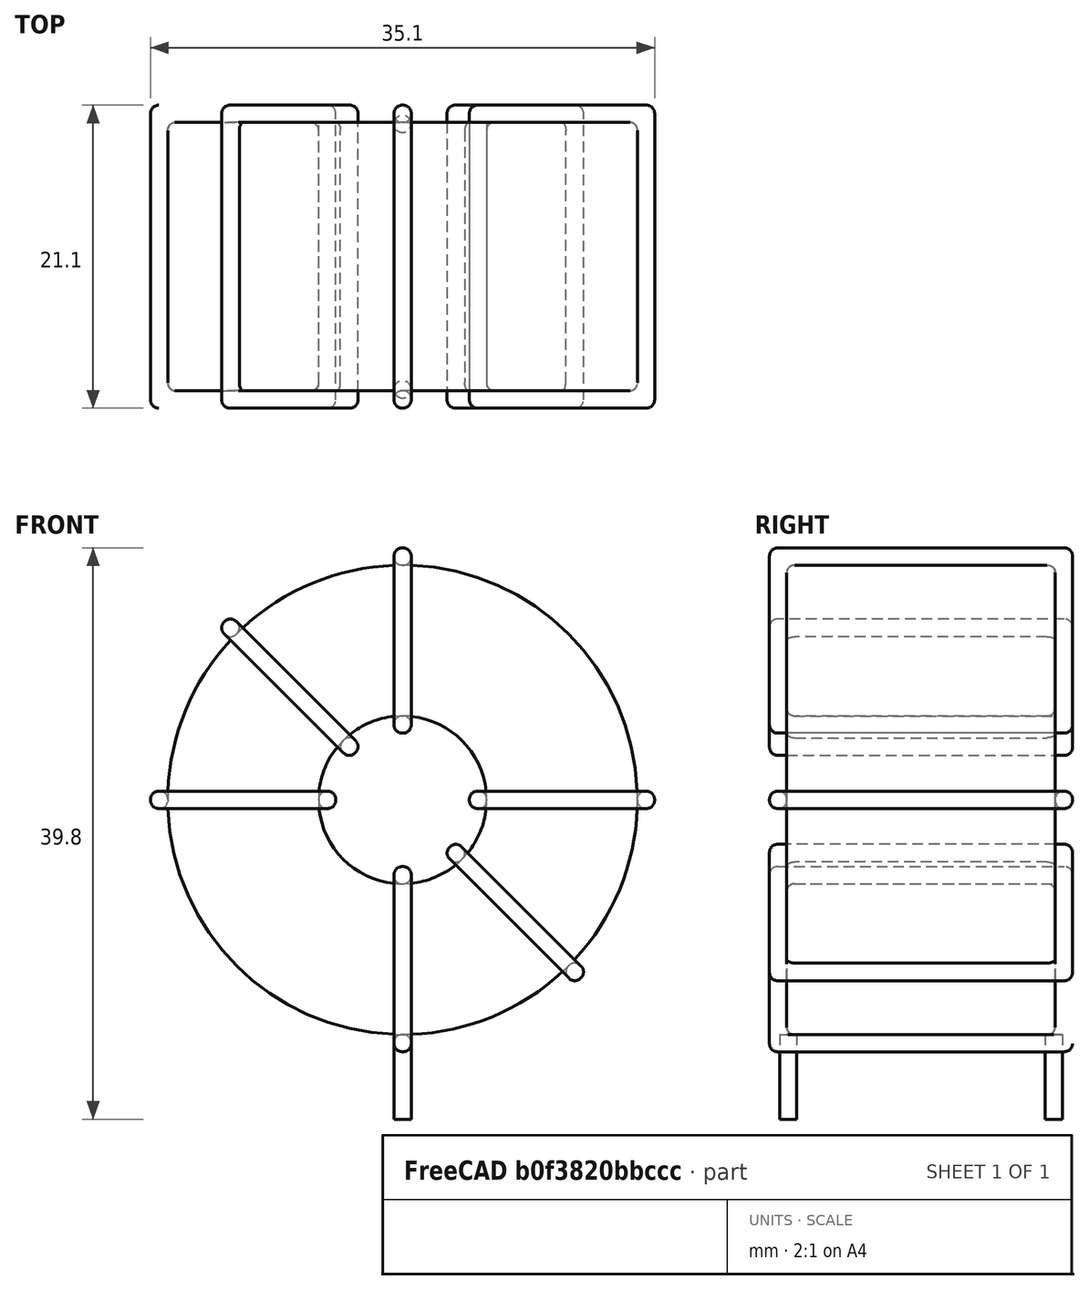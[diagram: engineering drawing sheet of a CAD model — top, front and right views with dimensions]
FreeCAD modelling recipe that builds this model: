
FCSTD DOCUMENT  (FreeCAD 0.16R6703 (Git))
Label: L_Toroid_Vertical_L35.1mm_W21.1mm_P18.50mm_Vishay_TJ6
License: All rights reserved
LicenseURL: http://en.wikipedia.org/wiki/All_rights_reserved
objects: Sketcher::SketchObject×6, PartDesign::Pad×6, PartDesign::Fillet×5, Spreadsheet::Sheet×1
note: 23 computed .brp shape members not serialized (recipe doc carries the construction recipe); baked Part::Feature solids carry a one-line shape summary decoded from their .brp

FEATURE [Spreadsheet::Sheet] Spreadsheet  label="dimensions"
  cells = A1=Wx; B1(Wx)=35.1; C1(WW)=11.7; D1=35.1; A2=Wy; B2(Wy)=21.1; D2=21.1; A3=RM; B3(RMx)=18.5; C3(RMy)=0; A4=d_wire; B4(d_wire)=1.2; A5=H; B5(H)=35.1; A6=offsetx; B6(offsetx)=17.55
FEATURE [Sketcher::SketchObject] Sketch
  Placement = pos=(0,-9.25,0) rot=(1,0,0;1.5708rad)
  expr: Placement.Base.y = -Spreadsheet.RMx / 2
  expr: Constraints[0] = Spreadsheet.Wx / 2 - Spreadsheet.d_wire
  expr: Constraints[4] = Spreadsheet.WW / 2
  expr: Constraints[2] = Spreadsheet.Wx / 2 + Spreadsheet.d_wire + 0.5
  sketch-geometry (2):
    g0: Circle CenterX=0 CenterY=19.25 CenterZ=0 NormalX=0 NormalY=0 NormalZ=1 Radius=16.35
    g1: Circle CenterX=0 CenterY=19.25 CenterZ=0 NormalX=0 NormalY=0 NormalZ=1 Radius=5.85
  constraints (5):
    c: Radius(g0) = 16.35
    c: DistanceX(g-1,g0) = 0
    c: DistanceY(g-1,g0) = 19.25
    c: Coincident(g1,g0)
    c: Radius(g1) = 5.85
FEATURE [PartDesign::Pad] Pad
  Length = 18.7
  Length2 = 100
  Midplane = true
  Placement = pos=(0,-9.25,0) rot=(1,0,0;1.5708rad)
  Sketch = -> Sketch
  Type = 0
  expr: Length = Spreadsheet.Wy - 2 * Spreadsheet.d_wire
FEATURE [Sketcher::SketchObject] Sketch001
  Placement = pos=(0,0,1.7) rot=(0,0,1;0rad)
  expr: Placement.Base.z = 0.5 + Spreadsheet.d_wire
  expr: Constraints[4] = Spreadsheet.RMy
  expr: Constraints[2] = -Spreadsheet.RMx
  expr: Constraints[1] = Spreadsheet.d_wire / 2
  sketch-geometry (2):
    g0: Circle CenterX=0 CenterY=0 CenterZ=0 NormalX=0 NormalY=0 NormalZ=1 Radius=0.6
    g1: Circle CenterX=0 CenterY=-18.5 CenterZ=0 NormalX=0 NormalY=0 NormalZ=1 Radius=0.6
  constraints (5):
    c: Equal(g0,g1)
    c: Radius(g0) = 0.6
    c: DistanceY(g-1,g1) = -18.5
    c: Coincident(g0,g-1)
    c: DistanceX(g-1,g1) = 0
FEATURE [PartDesign::Pad] Pad001
  Length = 1.2
  Length2 = 4.7
  Placement = pos=(0,0,1.7) rot=(0,0,1;0rad)
  Reversed = true
  Sketch = -> Sketch001
  Type = 4
  expr: Length2 = 3.5 + Spreadsheet.d_wire
  expr: Length = Spreadsheet.d_wire
FEATURE [PartDesign::Fillet] Fillet
  Base = -> Pad [Edge6,Edge3,Edge2]
  Placement = pos=(0,-9.25,0) rot=(1,0,0;1.5708rad)
  Radius = 0.5
FEATURE [Sketcher::SketchObject] Sketch003
  Placement = pos=(0,1.3,19.25) rot=(1,0,0;3.14159rad)
  expr: Constraints[18] = Spreadsheet.d_wire
  expr: Constraints[16] = Spreadsheet.d_wire
  expr: Constraints[19] = Spreadsheet.d_wire
  expr: Constraints[17] = Spreadsheet.d_wire
  expr: Placement.Base.y = -1 * (Spreadsheet.RMx - Spreadsheet.Wy) / 2
  expr: Constraints[21] = (Spreadsheet.Wx - Spreadsheet.WW) / 2 - Spreadsheet.d_wire
  expr: Constraints[22] = Spreadsheet.Wx / 2 - Spreadsheet.d_wire
  expr: Constraints[43] = Spreadsheet.d_wire
  expr: Constraints[48] = Spreadsheet.Wx - Spreadsheet.d_wire * 2
  expr: Constraints[49] = Spreadsheet.Wy
  expr: Placement.Base.z = Spreadsheet.Wx / 2 + Spreadsheet.d_wire + 0.5
  sketch-geometry (16):
    g0: LineSegment StartX=-4.65 StartY=0 StartZ=0 EndX=-17.55 EndY=0 EndZ=0
    g1: LineSegment StartX=-17.55 StartY=0 StartZ=0 EndX=-17.55 EndY=21.1 EndZ=0
    g2: LineSegment StartX=-17.55 StartY=21.1 StartZ=0 EndX=-4.65 EndY=21.1 EndZ=0
    g3: LineSegment StartX=-4.65 StartY=21.1 StartZ=0 EndX=-4.65 EndY=0 EndZ=0
    g4: LineSegment StartX=-16.35 StartY=19.9 StartZ=0 EndX=-5.85 EndY=19.9 EndZ=0
    g5: LineSegment StartX=-5.85 StartY=19.9 StartZ=0 EndX=-5.85 EndY=1.2 EndZ=0
    g6: LineSegment StartX=-5.85 StartY=1.2 StartZ=0 EndX=-16.35 EndY=1.2 EndZ=0
    g7: LineSegment StartX=-16.35 StartY=1.2 StartZ=0 EndX=-16.35 EndY=19.9 EndZ=0
    g8: LineSegment StartX=4.65 StartY=21.1 StartZ=0 EndX=17.55 EndY=21.1 EndZ=0
    g9: LineSegment StartX=17.55 StartY=21.1 StartZ=0 EndX=17.55 EndY=0 EndZ=0
    g10: LineSegment StartX=17.55 StartY=0 StartZ=0 EndX=4.65 EndY=0 EndZ=0
    g11: LineSegment StartX=4.65 StartY=0 StartZ=0 EndX=4.65 EndY=21.1 EndZ=0
    g12: LineSegment StartX=5.85 StartY=19.9 StartZ=0 EndX=16.35 EndY=19.9 EndZ=0
    g13: LineSegment StartX=16.35 StartY=19.9 StartZ=0 EndX=16.35 EndY=1.2 EndZ=0
    g14: LineSegment StartX=16.35 StartY=1.2 StartZ=0 EndX=5.85 EndY=1.2 EndZ=0
    g15: LineSegment StartX=5.85 StartY=1.2 StartZ=0 EndX=5.85 EndY=19.9 EndZ=0
  constraints (50):
    c: Horizontal(g0)
    c: Coincident(g1,g0)
    c: Vertical(g1)
    c: Coincident(g2,g1)
    c: Horizontal(g2)
    c: Coincident(g3,g2)
    c: Coincident(g3,g0)
    c: Vertical(g3)
    c: Coincident(g4,g5)
    c: Coincident(g5,g6)
    c: Coincident(g6,g7)
    c: Coincident(g7,g4)
    c: Horizontal(g4)
    c: Horizontal(g6)
    c: Vertical(g5)
    c: Vertical(g7)
    c: DistanceX(g1,g4) = 1.2
    c: DistanceY(g4,g1) = 1.2
    c: DistanceX(g5,g0) = 1.2
    c: DistanceY(g0,g5) = 1.2
    c: DistanceY(g-1,g0) = 0
    c: DistanceX(g6,g6) = 10.5
    c: DistanceX(g6,g-1) = 16.35
    c: Coincident(g8,g9)
    c: Coincident(g9,g10)
    c: Coincident(g10,g11)
    c: Coincident(g11,g8)
    c: Horizontal(g8)
    c: Horizontal(g10)
    c: Vertical(g9)
    c: Vertical(g11)
    c: Coincident(g12,g13)
    c: Coincident(g13,g14)
    c: Coincident(g14,g15)
    c: Coincident(g15,g12)
    c: Horizontal(g12)
    c: Horizontal(g14)
    c: Vertical(g13)
    c: Vertical(g15)
    c: DistanceY(g8,g2) = 0
    c: DistanceY(g10,g0) = 0
    c: DistanceY(g14,g5) = 0
    c: DistanceY(g12,g4) = 0
    c: DistanceX(g8,g12) = 1.2
    c: Equal(g8,g2)
    c: Equal(g12,g4)
    c: Equal(g9,g1)
    c: Equal(g13,g7)
    c: DistanceX(g4,g12) = 32.7
    c: DistanceY(g0,g1) = 21.1
FEATURE [PartDesign::Pad] Pad002
  Length = 1.2
  Length2 = 100
  Midplane = true
  Placement = pos=(0,1.3,19.25) rot=(1,0,0;3.14159rad)
  Sketch = -> Sketch003
  Type = 0
  expr: Length = Spreadsheet.d_wire
FEATURE [PartDesign::Fillet] Fillet001
  Base = -> Pad002 [Edge38,Edge41,Edge42,Edge43,Edge29,Edge32,Edge33,Edge34,Edge25,Edge35,Edge36,Edge13,Edge14,Edge15,Edge16,Edge17,Edge18,Edge19,Edge1,Edge2,Edge3,Edge4,Edge5,Edge6,Edge7,Edge37,Edge39,Edge40,Edge20,Edge23,Edge24,Edge21,Edge22,Edge8,Edge9,Edge10,Edge11,Edge12,Edge26,Edge27,+8 more]
  Placement = pos=(0,1.3,19.25) rot=(1,0,0;3.14159rad)
  Radius = 0.564
  expr: Radius = Spreadsheet.d_wire * 0.47
FEATURE [Sketcher::SketchObject] Sketch004
  Placement = pos=(0,1.3,19.25) rot=(0.92388,0,0.382683;3.14159rad)
  expr: Constraints[18] = Spreadsheet.d_wire
  expr: Constraints[16] = Spreadsheet.d_wire
  expr: Constraints[19] = Spreadsheet.d_wire
  expr: Constraints[17] = Spreadsheet.d_wire
  expr: Placement.Base.y = -1 * (Spreadsheet.RMx - Spreadsheet.Wy) / 2
  expr: Constraints[21] = (Spreadsheet.Wx - Spreadsheet.WW) / 2 - Spreadsheet.d_wire
  expr: Constraints[22] = Spreadsheet.Wx / 2 - Spreadsheet.d_wire
  expr: Constraints[43] = Spreadsheet.d_wire
  expr: Constraints[48] = Spreadsheet.Wx - 2 * Spreadsheet.d_wire
  expr: Constraints[49] = Spreadsheet.Wy
  expr: Placement.Base.z = Spreadsheet.Wx / 2 + Spreadsheet.d_wire + 0.5
  sketch-geometry (16):
    g0: LineSegment StartX=-4.65 StartY=0 StartZ=0 EndX=-17.55 EndY=0 EndZ=0
    g1: LineSegment StartX=-17.55 StartY=0 StartZ=0 EndX=-17.55 EndY=21.1 EndZ=0
    g2: LineSegment StartX=-17.55 StartY=21.1 StartZ=0 EndX=-4.65 EndY=21.1 EndZ=0
    g3: LineSegment StartX=-4.65 StartY=21.1 StartZ=0 EndX=-4.65 EndY=0 EndZ=0
    g4: LineSegment StartX=-16.35 StartY=19.9 StartZ=0 EndX=-5.85 EndY=19.9 EndZ=0
    g5: LineSegment StartX=-5.85 StartY=19.9 StartZ=0 EndX=-5.85 EndY=1.2 EndZ=0
    g6: LineSegment StartX=-5.85 StartY=1.2 StartZ=0 EndX=-16.35 EndY=1.2 EndZ=0
    g7: LineSegment StartX=-16.35 StartY=1.2 StartZ=0 EndX=-16.35 EndY=19.9 EndZ=0
    g8: LineSegment StartX=4.65 StartY=21.1 StartZ=0 EndX=17.55 EndY=21.1 EndZ=0
    g9: LineSegment StartX=17.55 StartY=21.1 StartZ=0 EndX=17.55 EndY=0 EndZ=0
    g10: LineSegment StartX=17.55 StartY=0 StartZ=0 EndX=4.65 EndY=0 EndZ=0
    g11: LineSegment StartX=4.65 StartY=0 StartZ=0 EndX=4.65 EndY=21.1 EndZ=0
    g12: LineSegment StartX=5.85 StartY=19.9 StartZ=0 EndX=16.35 EndY=19.9 EndZ=0
    g13: LineSegment StartX=16.35 StartY=19.9 StartZ=0 EndX=16.35 EndY=1.2 EndZ=0
    g14: LineSegment StartX=16.35 StartY=1.2 StartZ=0 EndX=5.85 EndY=1.2 EndZ=0
    g15: LineSegment StartX=5.85 StartY=1.2 StartZ=0 EndX=5.85 EndY=19.9 EndZ=0
  constraints (50):
    c: Horizontal(g0)
    c: Coincident(g1,g0)
    c: Vertical(g1)
    c: Coincident(g2,g1)
    c: Horizontal(g2)
    c: Coincident(g3,g2)
    c: Coincident(g3,g0)
    c: Vertical(g3)
    c: Coincident(g4,g5)
    c: Coincident(g5,g6)
    c: Coincident(g6,g7)
    c: Coincident(g7,g4)
    c: Horizontal(g4)
    c: Horizontal(g6)
    c: Vertical(g5)
    c: Vertical(g7)
    c: DistanceX(g1,g4) = 1.2
    c: DistanceY(g4,g1) = 1.2
    c: DistanceX(g5,g0) = 1.2
    c: DistanceY(g0,g5) = 1.2
    c: DistanceY(g-1,g0) = 0
    c: DistanceX(g6,g6) = 10.5
    c: DistanceX(g6,g-1) = 16.35
    c: Coincident(g8,g9)
    c: Coincident(g9,g10)
    c: Coincident(g10,g11)
    c: Coincident(g11,g8)
    c: Horizontal(g8)
    c: Horizontal(g10)
    c: Vertical(g9)
    c: Vertical(g11)
    c: Coincident(g12,g13)
    c: Coincident(g13,g14)
    c: Coincident(g14,g15)
    c: Coincident(g15,g12)
    c: Horizontal(g12)
    c: Horizontal(g14)
    c: Vertical(g13)
    c: Vertical(g15)
    c: DistanceY(g8,g2) = 0
    c: DistanceY(g10,g0) = 0
    c: DistanceY(g14,g5) = 0
    c: DistanceY(g12,g4) = 0
    c: DistanceX(g8,g12) = 1.2
    c: Equal(g8,g2)
    c: Equal(g12,g4)
    c: Equal(g9,g1)
    c: Equal(g13,g7)
    c: DistanceX(g4,g12) = 32.7
    c: DistanceY(g0,g1) = 21.1
FEATURE [PartDesign::Pad] Pad003
  Length = 1.2
  Length2 = 100
  Midplane = true
  Placement = pos=(0,1.3,19.25) rot=(0.92388,0,0.382683;3.14159rad)
  Sketch = -> Sketch004
  Type = 0
  expr: Length = Spreadsheet.d_wire
FEATURE [PartDesign::Fillet] Fillet002
  Base = -> Pad003 [Edge38,Edge41,Edge42,Edge43,Edge29,Edge32,Edge33,Edge34,Edge25,Edge35,Edge36,Edge13,Edge14,Edge15,Edge16,Edge17,Edge18,Edge19,Edge1,Edge2,Edge3,Edge4,Edge5,Edge6,Edge7,Edge37,Edge39,Edge40,Edge20,Edge23,Edge24,Edge21,Edge22,Edge8,Edge9,Edge10,Edge11,Edge12,Edge26,Edge27,+8 more]
  Placement = pos=(0,1.3,19.25) rot=(0.92388,0,0.382683;3.14159rad)
  Radius = 0.564
  expr: Radius = Spreadsheet.d_wire * 0.47
FEATURE [Sketcher::SketchObject] Sketch005
  Placement = pos=(0,1.3,19.25) rot=(0.92388,0,-0.382683;3.14159rad)
  expr: Constraints[18] = Spreadsheet.d_wire
  expr: Constraints[16] = Spreadsheet.d_wire
  expr: Constraints[19] = Spreadsheet.d_wire
  expr: Constraints[17] = Spreadsheet.d_wire
  expr: Placement.Base.y = -1 * (Spreadsheet.RMx - Spreadsheet.Wy) / 2
  expr: Constraints[21] = (Spreadsheet.Wx - Spreadsheet.WW) / 2 - Spreadsheet.d_wire
  expr: Constraints[22] = Spreadsheet.Wx / 2 - Spreadsheet.d_wire
  expr: Constraints[43] = Spreadsheet.d_wire
  expr: Constraints[48] = Spreadsheet.Wx - 2 * Spreadsheet.d_wire
  expr: Constraints[49] = Spreadsheet.Wy
  expr: Placement.Base.z = Spreadsheet.Wx / 2 + Spreadsheet.d_wire + 0.5
  sketch-geometry (16):
    g0: LineSegment StartX=-4.65 StartY=0 StartZ=0 EndX=-17.55 EndY=0 EndZ=0
    g1: LineSegment StartX=-17.55 StartY=0 StartZ=0 EndX=-17.55 EndY=21.1 EndZ=0
    g2: LineSegment StartX=-17.55 StartY=21.1 StartZ=0 EndX=-4.65 EndY=21.1 EndZ=0
    g3: LineSegment StartX=-4.65 StartY=21.1 StartZ=0 EndX=-4.65 EndY=0 EndZ=0
    g4: LineSegment StartX=-16.35 StartY=19.9 StartZ=0 EndX=-5.85 EndY=19.9 EndZ=0
    g5: LineSegment StartX=-5.85 StartY=19.9 StartZ=0 EndX=-5.85 EndY=1.2 EndZ=0
    g6: LineSegment StartX=-5.85 StartY=1.2 StartZ=0 EndX=-16.35 EndY=1.2 EndZ=0
    g7: LineSegment StartX=-16.35 StartY=1.2 StartZ=0 EndX=-16.35 EndY=19.9 EndZ=0
    g8: LineSegment StartX=4.65 StartY=21.1 StartZ=0 EndX=17.55 EndY=21.1 EndZ=0
    g9: LineSegment StartX=17.55 StartY=21.1 StartZ=0 EndX=17.55 EndY=0 EndZ=0
    g10: LineSegment StartX=17.55 StartY=0 StartZ=0 EndX=4.65 EndY=0 EndZ=0
    g11: LineSegment StartX=4.65 StartY=0 StartZ=0 EndX=4.65 EndY=21.1 EndZ=0
    g12: LineSegment StartX=5.85 StartY=19.9 StartZ=0 EndX=16.35 EndY=19.9 EndZ=0
    g13: LineSegment StartX=16.35 StartY=19.9 StartZ=0 EndX=16.35 EndY=1.2 EndZ=0
    g14: LineSegment StartX=16.35 StartY=1.2 StartZ=0 EndX=5.85 EndY=1.2 EndZ=0
    g15: LineSegment StartX=5.85 StartY=1.2 StartZ=0 EndX=5.85 EndY=19.9 EndZ=0
  constraints (50):
    c: Horizontal(g0)
    c: Coincident(g1,g0)
    c: Vertical(g1)
    c: Coincident(g2,g1)
    c: Horizontal(g2)
    c: Coincident(g3,g2)
    c: Coincident(g3,g0)
    c: Vertical(g3)
    c: Coincident(g4,g5)
    c: Coincident(g5,g6)
    c: Coincident(g6,g7)
    c: Coincident(g7,g4)
    c: Horizontal(g4)
    c: Horizontal(g6)
    c: Vertical(g5)
    c: Vertical(g7)
    c: DistanceX(g1,g4) = 1.2
    c: DistanceY(g4,g1) = 1.2
    c: DistanceX(g5,g0) = 1.2
    c: DistanceY(g0,g5) = 1.2
    c: DistanceY(g-1,g0) = 0
    c: DistanceX(g6,g6) = 10.5
    c: DistanceX(g6,g-1) = 16.35
    c: Coincident(g8,g9)
    c: Coincident(g9,g10)
    c: Coincident(g10,g11)
    c: Coincident(g11,g8)
    c: Horizontal(g8)
    c: Horizontal(g10)
    c: Vertical(g9)
    c: Vertical(g11)
    c: Coincident(g12,g13)
    c: Coincident(g13,g14)
    c: Coincident(g14,g15)
    c: Coincident(g15,g12)
    c: Horizontal(g12)
    c: Horizontal(g14)
    c: Vertical(g13)
    c: Vertical(g15)
    c: DistanceY(g8,g2) = 0
    c: DistanceY(g10,g0) = 0
    c: DistanceY(g14,g5) = 0
    c: DistanceY(g12,g4) = 0
    c: DistanceX(g8,g12) = 1.2
    c: Equal(g8,g2)
    c: Equal(g12,g4)
    c: Equal(g9,g1)
    c: Equal(g13,g7)
    c: DistanceX(g4,g12) = 32.7
    c: DistanceY(g0,g1) = 21.1
FEATURE [PartDesign::Pad] Pad004
  Length = 1.2
  Length2 = 100
  Midplane = true
  Placement = pos=(0,1.3,19.25) rot=(0.92388,0,-0.382683;3.14159rad)
  Sketch = -> Sketch005
  Type = 0
  expr: Length = Spreadsheet.d_wire
FEATURE [PartDesign::Fillet] Fillet003
  Base = -> Pad004 [Edge38,Edge41,Edge42,Edge43,Edge29,Edge32,Edge33,Edge34,Edge25,Edge35,Edge36,Edge13,Edge14,Edge15,Edge16,Edge17,Edge18,Edge19,Edge1,Edge2,Edge3,Edge4,Edge5,Edge6,Edge7,Edge37,Edge39,Edge40,Edge20,Edge23,Edge24,Edge21,Edge22,Edge8,Edge9,Edge10,Edge11,Edge12,Edge26,Edge27,+8 more]
  Placement = pos=(0,1.3,19.25) rot=(0.92388,0,-0.382683;3.14159rad)
  Radius = 0.564
  expr: Radius = Spreadsheet.d_wire * 0.47
FEATURE [Sketcher::SketchObject] Sketch006
  Placement = pos=(0,1.3,19.25) rot=(0.707107,0,0.707107;3.14159rad)
  expr: Constraints[18] = Spreadsheet.d_wire
  expr: Constraints[16] = Spreadsheet.d_wire
  expr: Constraints[19] = Spreadsheet.d_wire
  expr: Constraints[17] = Spreadsheet.d_wire
  expr: Placement.Base.y = -1 * (Spreadsheet.RMx - Spreadsheet.Wy) / 2
  expr: Constraints[21] = (Spreadsheet.Wx - Spreadsheet.WW) / 2 - Spreadsheet.d_wire
  expr: Constraints[22] = Spreadsheet.Wx / 2 - Spreadsheet.d_wire
  expr: Constraints[43] = Spreadsheet.d_wire
  expr: Constraints[48] = Spreadsheet.Wx - Spreadsheet.d_wire * 2
  expr: Constraints[49] = Spreadsheet.Wy
  expr: Placement.Base.z = Spreadsheet.Wx / 2 + Spreadsheet.d_wire + 0.5
  sketch-geometry (16):
    g0: LineSegment StartX=-4.65 StartY=0 StartZ=0 EndX=-17.55 EndY=0 EndZ=0
    g1: LineSegment StartX=-17.55 StartY=0 StartZ=0 EndX=-17.55 EndY=21.1 EndZ=0
    g2: LineSegment StartX=-17.55 StartY=21.1 StartZ=0 EndX=-4.65 EndY=21.1 EndZ=0
    g3: LineSegment StartX=-4.65 StartY=21.1 StartZ=0 EndX=-4.65 EndY=0 EndZ=0
    g4: LineSegment StartX=-16.35 StartY=19.9 StartZ=0 EndX=-5.85 EndY=19.9 EndZ=0
    g5: LineSegment StartX=-5.85 StartY=19.9 StartZ=0 EndX=-5.85 EndY=1.2 EndZ=0
    g6: LineSegment StartX=-5.85 StartY=1.2 StartZ=0 EndX=-16.35 EndY=1.2 EndZ=0
    g7: LineSegment StartX=-16.35 StartY=1.2 StartZ=0 EndX=-16.35 EndY=19.9 EndZ=0
    g8: LineSegment StartX=4.65 StartY=21.1 StartZ=0 EndX=17.55 EndY=21.1 EndZ=0
    g9: LineSegment StartX=17.55 StartY=21.1 StartZ=0 EndX=17.55 EndY=0 EndZ=0
    g10: LineSegment StartX=17.55 StartY=0 StartZ=0 EndX=4.65 EndY=0 EndZ=0
    g11: LineSegment StartX=4.65 StartY=0 StartZ=0 EndX=4.65 EndY=21.1 EndZ=0
    g12: LineSegment StartX=5.85 StartY=19.9 StartZ=0 EndX=16.35 EndY=19.9 EndZ=0
    g13: LineSegment StartX=16.35 StartY=19.9 StartZ=0 EndX=16.35 EndY=1.2 EndZ=0
    g14: LineSegment StartX=16.35 StartY=1.2 StartZ=0 EndX=5.85 EndY=1.2 EndZ=0
    g15: LineSegment StartX=5.85 StartY=1.2 StartZ=0 EndX=5.85 EndY=19.9 EndZ=0
  constraints (50):
    c: Horizontal(g0)
    c: Coincident(g1,g0)
    c: Vertical(g1)
    c: Coincident(g2,g1)
    c: Horizontal(g2)
    c: Coincident(g3,g2)
    c: Coincident(g3,g0)
    c: Vertical(g3)
    c: Coincident(g4,g5)
    c: Coincident(g5,g6)
    c: Coincident(g6,g7)
    c: Coincident(g7,g4)
    c: Horizontal(g4)
    c: Horizontal(g6)
    c: Vertical(g5)
    c: Vertical(g7)
    c: DistanceX(g1,g4) = 1.2
    c: DistanceY(g4,g1) = 1.2
    c: DistanceX(g5,g0) = 1.2
    c: DistanceY(g0,g5) = 1.2
    c: DistanceY(g-1,g0) = 0
    c: DistanceX(g6,g6) = 10.5
    c: DistanceX(g6,g-1) = 16.35
    c: Coincident(g8,g9)
    c: Coincident(g9,g10)
    c: Coincident(g10,g11)
    c: Coincident(g11,g8)
    c: Horizontal(g8)
    c: Horizontal(g10)
    c: Vertical(g9)
    c: Vertical(g11)
    c: Coincident(g12,g13)
    c: Coincident(g13,g14)
    c: Coincident(g14,g15)
    c: Coincident(g15,g12)
    c: Horizontal(g12)
    c: Horizontal(g14)
    c: Vertical(g13)
    c: Vertical(g15)
    c: DistanceY(g8,g2) = 0
    c: DistanceY(g10,g0) = 0
    c: DistanceY(g14,g5) = 0
    c: DistanceY(g12,g4) = 0
    c: DistanceX(g8,g12) = 1.2
    c: Equal(g8,g2)
    c: Equal(g12,g4)
    c: Equal(g9,g1)
    c: Equal(g13,g7)
    c: DistanceX(g4,g12) = 32.7
    c: DistanceY(g0,g1) = 21.1
FEATURE [PartDesign::Pad] Pad005
  Length = 1.2
  Length2 = 100
  Midplane = true
  Placement = pos=(0,1.3,19.25) rot=(0.707107,0,0.707107;3.14159rad)
  Sketch = -> Sketch006
  Type = 0
  expr: Length = Spreadsheet.d_wire
FEATURE [PartDesign::Fillet] Fillet004
  Base = -> Pad005 [Edge38,Edge41,Edge42,Edge43,Edge29,Edge32,Edge33,Edge34,Edge25,Edge35,Edge36,Edge13,Edge14,Edge15,Edge16,Edge17,Edge18,Edge19,Edge1,Edge2,Edge3,Edge4,Edge5,Edge6,Edge7,Edge37,Edge39,Edge40,Edge20,Edge23,Edge24,Edge21,Edge22,Edge8,Edge9,Edge10,Edge11,Edge12,Edge26,Edge27,+8 more]
  Placement = pos=(0,1.3,19.25) rot=(0.707107,0,0.707107;3.14159rad)
  Radius = 0.564
  expr: Radius = Spreadsheet.d_wire * 0.47
